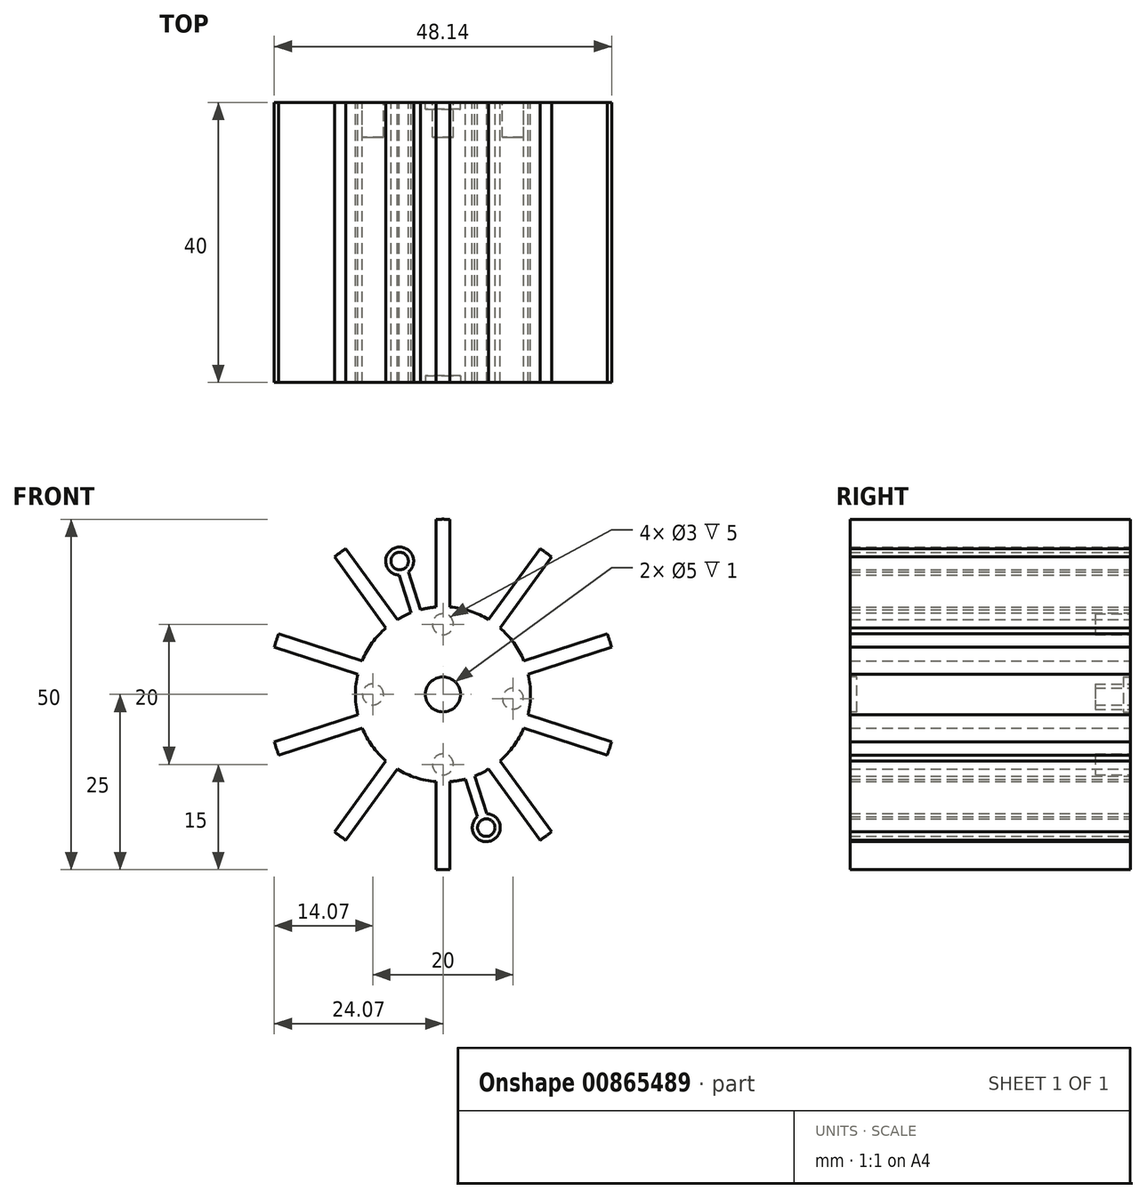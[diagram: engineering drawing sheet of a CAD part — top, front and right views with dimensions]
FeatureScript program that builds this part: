
annotation { "Feature Type Name" : "Feature", "Feature Type Description" : "" }
export const myFeature = defineFeature(function(context is Context, id is Id, definition is map)
    precondition{}
    {
        {
            var Q0;
            Q0=qCreatedBy(makeId("Front.planeOp"),FACE);
            var sketch = newSketch(context, id + "F0", { "sketchPlane" : qUnion([Q0])});
            skCircle(sketch, "E0", {"center": v(0, 0) * mm, "radius": 25 * mm});
            skSolve(sketch);
        }
        {
            var Q0;
            Q0 = qSketchRegion(id + "F0", true);
            extrude(context, id + "F1", {"entities" : qUnion([Q0]), "depth" : 40 * mm, "offsetDistance" : 25 * mm});
        }
        {
            var Q0;
            Q0=makeQuery(id+"F1.opExtrude","CAP_FACE",FACE,{"disambiguationData":[OSD([sQuery(id+"F0.wireOp",EDGE,"E0")])],"isStart":true});
            var sketch = newSketch(context, id + "F2", { "sketchPlane" : qUnion([Q0])});
            skCircle(sketch, "E1", {"center": v(0, 0) * mm, "radius": 2.5 * mm});
            skSolve(sketch);
        }
        {
            var Q0;
            Q0 = qSketchRegion(id + "F2", true);
            extrude(context, id + "F3", {"entities" : qUnion([Q0]), "operationType" : NewBodyOperationType.REMOVE, "oppositeDirection" : true, "depth" : 1 * mm, "offsetDistance" : 25 * mm});
        }
        {
            var Q0;
            Q0=makeQuery(id+"F1.opExtrude","CAP_FACE",FACE,{"disambiguationData":[OSD([sQuery(id+"F0.wireOp",EDGE,"E0")])],"isStart":true});
            var sketch = newSketch(context, id + "F4", { "sketchPlane" : qUnion([Q0])});
            skCircle(sketch, "E2", {"center": v(0, 0) * mm, "radius": 12.5 * mm});
            skLineSegment(sketch, "E3", {"start": v(1, 12.46) * mm, "end": v(1, 24.98) * mm});
            skLineSegment(sketch, "E4", {"start": v(-1, 12.46) * mm, "end": v(-1, 24.98) * mm});
            skLineSegment(sketch, "E5.1.0", {"start": v(-6.51, 10.67) * mm, "end": v(-13.87, 20.8) * mm});
            skLineSegment(sketch, "E5.1.1", {"start": v(-8.13, 9.5) * mm, "end": v(-15.5, 19.62) * mm});
            skLineSegment(sketch, "E5.2.0", {"start": v(-11.54, 4.8) * mm, "end": v(-23.45, 8.67) * mm});
            skLineSegment(sketch, "E5.2.1", {"start": v(-12.16, 2.9) * mm, "end": v(-24.07, 6.77) * mm});
            skLineSegment(sketch, "E5.3.0", {"start": v(-12.16, -2.9) * mm, "end": v(-24.07, -6.77) * mm});
            skLineSegment(sketch, "E5.3.1", {"start": v(-11.54, -4.8) * mm, "end": v(-23.45, -8.67) * mm});
            skLineSegment(sketch, "E5.4.0", {"start": v(-8.13, -9.5) * mm, "end": v(-15.5, -19.62) * mm});
            skLineSegment(sketch, "E5.4.1", {"start": v(-6.51, -10.67) * mm, "end": v(-13.87, -20.8) * mm});
            skLineSegment(sketch, "E5.5.0", {"start": v(-1, -12.46) * mm, "end": v(-1, -24.98) * mm});
            skLineSegment(sketch, "E5.5.1", {"start": v(1, -12.46) * mm, "end": v(1, -24.98) * mm});
            skLineSegment(sketch, "E5.6.0", {"start": v(6.51, -10.67) * mm, "end": v(13.87, -20.8) * mm});
            skLineSegment(sketch, "E5.6.1", {"start": v(8.13, -9.5) * mm, "end": v(15.5, -19.62) * mm});
            skLineSegment(sketch, "E5.7.0", {"start": v(11.54, -4.8) * mm, "end": v(23.45, -8.67) * mm});
            skLineSegment(sketch, "E5.7.1", {"start": v(12.16, -2.9) * mm, "end": v(24.07, -6.77) * mm});
            skLineSegment(sketch, "E5.8.0", {"start": v(12.16, 2.9) * mm, "end": v(24.07, 6.77) * mm});
            skLineSegment(sketch, "E5.8.1", {"start": v(11.54, 4.8) * mm, "end": v(23.45, 8.67) * mm});
            skLineSegment(sketch, "E5.9.0", {"start": v(8.13, 9.5) * mm, "end": v(15.5, 19.62) * mm});
            skLineSegment(sketch, "E5.9.1", {"start": v(6.51, 10.67) * mm, "end": v(13.87, 20.8) * mm});
            skCircle(sketch, "E6", {"center": v(0, 0) * mm, "radius": 25 * mm});
            skSolve(sketch);
        }
        {
            var Q0;
            {var subQ0=sQuery(id+"F4.wireOp",EDGE,"E5.8.1");Q0=makeQuery(id+"F4.imprint","IMPRINT",FACE,{"disambiguationData":[TD([[makeQuery(id+"F4.imprint","IMPRINT",EDGE,{"derivedFrom":subQ0}),1.0]])]});}
            var Q1;
            {var subQ0=sQuery(id+"F4.wireOp",EDGE,"E3");Q1=makeQuery(id+"F4.imprint","IMPRINT",FACE,{"disambiguationData":[TD([[makeQuery(id+"F4.imprint","IMPRINT",EDGE,{"derivedFrom":subQ0}),-1.0]])]});}
            var Q2;
            {var subQ0=sQuery(id+"F4.wireOp",EDGE,"E4");Q2=makeQuery(id+"F4.imprint","IMPRINT",FACE,{"disambiguationData":[TD([[makeQuery(id+"F4.imprint","IMPRINT",EDGE,{"derivedFrom":subQ0}),1.0]])]});}
            var Q3;
            {var subQ0=sQuery(id+"F4.wireOp",EDGE,"E5.1.1");Q3=makeQuery(id+"F4.imprint","IMPRINT",FACE,{"disambiguationData":[TD([[makeQuery(id+"F4.imprint","IMPRINT",EDGE,{"derivedFrom":subQ0}),1.0]])]});}
            var Q4;
            {var subQ0=sQuery(id+"F4.wireOp",EDGE,"E5.2.1");Q4=makeQuery(id+"F4.imprint","IMPRINT",FACE,{"disambiguationData":[TD([[makeQuery(id+"F4.imprint","IMPRINT",EDGE,{"derivedFrom":subQ0}),1.0]])]});}
            var Q5;
            {var subQ0=sQuery(id+"F4.wireOp",EDGE,"E5.3.1");Q5=makeQuery(id+"F4.imprint","IMPRINT",FACE,{"disambiguationData":[TD([[makeQuery(id+"F4.imprint","IMPRINT",EDGE,{"derivedFrom":subQ0}),1.0]])]});}
            var Q6;
            {var subQ0=sQuery(id+"F4.wireOp",EDGE,"E5.4.1");Q6=makeQuery(id+"F4.imprint","IMPRINT",FACE,{"disambiguationData":[TD([[makeQuery(id+"F4.imprint","IMPRINT",EDGE,{"derivedFrom":subQ0}),1.0]])]});}
            var Q7;
            {var subQ0=sQuery(id+"F4.wireOp",EDGE,"E5.5.1");Q7=makeQuery(id+"F4.imprint","IMPRINT",FACE,{"disambiguationData":[TD([[makeQuery(id+"F4.imprint","IMPRINT",EDGE,{"derivedFrom":subQ0}),1.0]])]});}
            var Q8;
            {var subQ0=sQuery(id+"F4.wireOp",EDGE,"E5.6.1");Q8=makeQuery(id+"F4.imprint","IMPRINT",FACE,{"disambiguationData":[TD([[makeQuery(id+"F4.imprint","IMPRINT",EDGE,{"derivedFrom":subQ0}),1.0]])]});}
            var Q9;
            {var subQ0=sQuery(id+"F4.wireOp",EDGE,"E5.7.1");Q9=makeQuery(id+"F4.imprint","IMPRINT",FACE,{"disambiguationData":[TD([[makeQuery(id+"F4.imprint","IMPRINT",EDGE,{"derivedFrom":subQ0}),1.0]])]});}
            extrude(context, id + "F5", {"entities" : qUnion([Q0, Q1, Q2, Q3, Q4, Q5, Q6, Q7, Q8, Q9]), "operationType" : NewBodyOperationType.REMOVE, "endBound" : BoundingType.THROUGH_ALL, "oppositeDirection" : true, "depth" : 25 * mm, "offsetDistance" : 25 * mm});
        }
        {
            var Q0;
            Q0=makeQuery(id+"F1.opExtrude","CAP_FACE",FACE,{"disambiguationData":[OSD([sQuery(id+"F0.wireOp",EDGE,"E0")])],"isStart":true});
            var sketch = newSketch(context, id + "F6", { "sketchPlane" : qUnion([Q0])});
            skLineSegment(sketch, "E7", {"start": v(0, 0) * mm, "end": v(7.78, 23.93) * mm});
            skLineSegment(sketch, "E8", {"start": v(3.2, 12.09) * mm, "end": v(5.51, 19.24) * mm});
            skLineSegment(sketch, "E9", {"start": v(5.51, 19.24) * mm, "end": v(6.85, 18.8) * mm});
            skLineSegment(sketch, "E10", {"start": v(6.85, 18.8) * mm, "end": v(4.52, 11.65) * mm});
            skCircle(sketch, "E11", {"center": v(6.18, 19.02) * mm, "radius": 2 * mm});
            skCircle(sketch, "E12", {"center": v(6.18, 19.02) * mm, "radius": 1.25 * mm});
            skLineSegment(sketch, "E13.1.0", {"start": v(-3.2, -12.09) * mm, "end": v(-5.51, -19.24) * mm});
            skLineSegment(sketch, "E13.1.1", {"start": v(-6.85, -18.8) * mm, "end": v(-4.52, -11.65) * mm});
            skCircle(sketch, "E13.1.2", {"center": v(-6.18, -19.02) * mm, "radius": 2 * mm});
            skCircle(sketch, "E13.1.3", {"center": v(-6.18, -19.02) * mm, "radius": 1.25 * mm});
            skPoint(sketch, "E13.center", {"position": v(0, 0) * mm});
            skCircle(sketch, "E14", {"center": v(0, 0) * mm, "radius": 12.5 * mm});
            skSolve(sketch);
        }
        {
            var Q0;
            Q0=makeQuery(id+"F6.imprint","IMPRINT",FACE,{"disambiguationData":[TD([[makeQuery(id+"F6.imprint","IMPRINT",EDGE,{"derivedFrom":makeQuery(id+"F3.boolean.opBoolean","COPY",EDGE,{"derivedFrom":makeQuery(id+"F3.opExtrude","CAP_EDGE",EDGE,{"disambiguationData":[OSD([sQuery(id+"F2.wireOp",EDGE,"E1")])],"isStart":true})})}),1.0]])]});
            var Q1;
            {var subQ0=sQuery(id+"F6.wireOp",EDGE,"E14");var subQ1=sQuery(id+"F6.wireOp",EDGE,"E13.1.0");var subQ2=makeQuery(id+"F6.imprint","INTERSECT",VERTEX,{"derivedFrom":[subQ1,subQ0]});Q1=makeQuery(id+"F6.imprint","IMPRINT",FACE,{"disambiguationData":[TD([[makeQuery(id+"F6.imprint","IMPRINT",EDGE,{"disambiguationData":[TD([[subQ2,-1.0]])],"derivedFrom":subQ1}),-1.0]])]});}
            var Q2;
            {var subQ0=sQuery(id+"F6.wireOp",EDGE,"E13.1.2");var subQ1=sQuery(id+"F6.wireOp",EDGE,"E13.1.0");var subQ2=makeQuery(id+"F6.imprint","INTERSECT",VERTEX,{"derivedFrom":[subQ1,subQ0]});Q2=makeQuery(id+"F6.imprint","IMPRINT",FACE,{"disambiguationData":[TD([[makeQuery(id+"F6.imprint","IMPRINT",EDGE,{"disambiguationData":[TD([[subQ2,-1.0]])],"derivedFrom":subQ1}),1.0]])]});}
            var Q3;
            {var subQ0=sQuery(id+"F6.wireOp",EDGE,"E14");var subQ1=sQuery(id+"F6.wireOp",EDGE,"E7");var subQ2=makeQuery(id+"F6.imprint","INTERSECT",VERTEX,{"derivedFrom":[subQ1,subQ0]});Q3=makeQuery(id+"F6.imprint","IMPRINT",FACE,{"disambiguationData":[TD([[makeQuery(id+"F6.imprint","IMPRINT",EDGE,{"disambiguationData":[TD([[subQ2,-1.0]])],"derivedFrom":subQ1}),1.0]])]});}
            var Q4;
            {var subQ0=sQuery(id+"F6.wireOp",EDGE,"E14");var subQ1=sQuery(id+"F6.wireOp",EDGE,"E7");var subQ2=makeQuery(id+"F6.imprint","INTERSECT",VERTEX,{"derivedFrom":[subQ1,subQ0]});Q4=makeQuery(id+"F6.imprint","IMPRINT",FACE,{"disambiguationData":[TD([[makeQuery(id+"F6.imprint","IMPRINT",EDGE,{"disambiguationData":[TD([[subQ2,-1.0]])],"derivedFrom":subQ1}),-1.0]])]});}
            var Q5;
            {var subQ0=sQuery(id+"F6.wireOp",EDGE,"E11");var subQ1=sQuery(id+"F6.wireOp",EDGE,"E7");var subQ2=makeQuery(id+"F6.imprint","INTERSECT",VERTEX,{"disambiguationData":[OD(0.0)],"derivedFrom":[subQ1,subQ0]});Q5=makeQuery(id+"F6.imprint","IMPRINT",FACE,{"disambiguationData":[TD([[makeQuery(id+"F6.imprint","IMPRINT",EDGE,{"disambiguationData":[TD([[subQ2,1.0]])],"derivedFrom":subQ1}),1.0]])]});}
            var Q6;
            {var subQ0=sQuery(id+"F6.wireOp",EDGE,"E11");var subQ1=sQuery(id+"F6.wireOp",EDGE,"E7");var subQ2=makeQuery(id+"F6.imprint","INTERSECT",VERTEX,{"disambiguationData":[OD(0.0)],"derivedFrom":[subQ1,subQ0]});Q6=makeQuery(id+"F6.imprint","IMPRINT",FACE,{"disambiguationData":[TD([[makeQuery(id+"F6.imprint","IMPRINT",EDGE,{"disambiguationData":[TD([[subQ2,1.0]])],"derivedFrom":subQ1}),-1.0]])]});}
            var Q7;
            {var subQ0=sQuery(id+"F6.wireOp",EDGE,"E13.1.2");var subQ1=sQuery(id+"F6.wireOp",EDGE,"E13.1.0");var subQ2=makeQuery(id+"F6.imprint","INTERSECT",VERTEX,{"derivedFrom":[subQ1,subQ0]});Q7=makeQuery(id+"F6.imprint","IMPRINT",FACE,{"disambiguationData":[TD([[makeQuery(id+"F6.imprint","IMPRINT",EDGE,{"disambiguationData":[TD([[subQ2,-1.0]])],"derivedFrom":subQ1}),-1.0]])]});}
            var Q8;
            {var subQ0=sQuery(id+"F6.wireOp",EDGE,"E11");var subQ1=sQuery(id+"F6.wireOp",EDGE,"E7");var subQ2=makeQuery(id+"F6.imprint","INTERSECT",VERTEX,{"disambiguationData":[OD(1.0)],"derivedFrom":[subQ1,subQ0]});Q8=makeQuery(id+"F6.imprint","IMPRINT",FACE,{"disambiguationData":[TD([[makeQuery(id+"F6.imprint","IMPRINT",EDGE,{"disambiguationData":[TD([[subQ2,-1.0]])],"derivedFrom":subQ1}),1.0]])]});}
            var Q9;
            {var subQ0=sQuery(id+"F6.wireOp",EDGE,"E11");var subQ1=sQuery(id+"F6.wireOp",EDGE,"E7");var subQ2=makeQuery(id+"F6.imprint","INTERSECT",VERTEX,{"disambiguationData":[OD(1.0)],"derivedFrom":[subQ1,subQ0]});Q9=makeQuery(id+"F6.imprint","IMPRINT",FACE,{"disambiguationData":[TD([[makeQuery(id+"F6.imprint","IMPRINT",EDGE,{"disambiguationData":[TD([[subQ2,-1.0]])],"derivedFrom":subQ1}),-1.0]])]});}
            extrude(context, id + "F7", {"entities" : qUnion([Q0, Q1, Q2, Q3, Q4, Q5, Q6, Q7, Q8, Q9]), "operationType" : NewBodyOperationType.ADD, "oppositeDirection" : true, "depth" : 40 * mm, "offsetDistance" : 25 * mm});
        }
        {
            var Q0;
            {var subQ0=sQuery(id+"F6.wireOp",EDGE,"E14");Q0=makeQuery(id+"F7.boolean.opBoolean","MERGE",FACE,{"derivedFrom":[makeQuery(id+"F1.opExtrude","CAP_FACE",FACE,{"disambiguationData":[OSD([sQuery(id+"F0.wireOp",EDGE,"E0")])],"isStart":false}),makeQuery(id+"F7.opExtrude","CAP_FACE",FACE,{"disambiguationData":[OSD([sQuery(id+"F6.wireOp",EDGE,"E8"),sQuery(id+"F6.wireOp",EDGE,"E10"),sQuery(id+"F6.wireOp",EDGE,"E11"),sQuery(id+"F6.wireOp",EDGE,"E12"),subQ0])],"isStart":false}),makeQuery(id+"F7.opExtrude","CAP_FACE",FACE,{"disambiguationData":[OSD([sQuery(id+"F6.wireOp",EDGE,"E13.1.0"),sQuery(id+"F6.wireOp",EDGE,"E13.1.1"),sQuery(id+"F6.wireOp",EDGE,"E13.1.2"),sQuery(id+"F6.wireOp",EDGE,"E13.1.3"),subQ0])],"isStart":false})]});}
            var sketch = newSketch(context, id + "F8", { "sketchPlane" : qUnion([Q0])});
            skCircle(sketch, "E15", {"center": v(0, 0) * mm, "radius": 2.5 * mm});
            skSolve(sketch);
        }
        {
            var Q0;
            Q0 = qSketchRegion(id + "F8", true);
            extrude(context, id + "F9", {"entities" : qUnion([Q0]), "operationType" : NewBodyOperationType.REMOVE, "oppositeDirection" : true, "depth" : 1 * mm, "offsetDistance" : 25 * mm});
        }
        {
            var Q0;
            {var subQ0=sQuery(id+"F6.wireOp",EDGE,"E14");Q0=makeQuery(id+"F7.boolean.opBoolean","MERGE",FACE,{"derivedFrom":[makeQuery(id+"F1.opExtrude","CAP_FACE",FACE,{"disambiguationData":[OSD([sQuery(id+"F0.wireOp",EDGE,"E0")])],"isStart":true}),makeQuery(id+"F7.opExtrude","CAP_FACE",FACE,{"disambiguationData":[OSD([sQuery(id+"F6.wireOp",EDGE,"E8"),sQuery(id+"F6.wireOp",EDGE,"E10"),sQuery(id+"F6.wireOp",EDGE,"E11"),sQuery(id+"F6.wireOp",EDGE,"E12"),subQ0])],"isStart":true}),makeQuery(id+"F7.opExtrude","CAP_FACE",FACE,{"disambiguationData":[OSD([sQuery(id+"F6.wireOp",EDGE,"E13.1.0"),sQuery(id+"F6.wireOp",EDGE,"E13.1.1"),sQuery(id+"F6.wireOp",EDGE,"E13.1.2"),sQuery(id+"F6.wireOp",EDGE,"E13.1.3"),subQ0])],"isStart":true}),makeQuery(id+"F7.opExtrude","CAP_FACE",FACE,{"disambiguationData":[OSD([sQuery(id+"F2.wireOp",EDGE,"E1")])],"isStart":true})]});}
            var sketch = newSketch(context, id + "F10", { "sketchPlane" : qUnion([Q0])});
            skCircle(sketch, "E16", {"center": v(10, 0) * mm, "radius": 1.5 * mm});
            skCircle(sketch, "E17", {"center": v(-10, -0.62) * mm, "radius": 1.5 * mm});
            skCircle(sketch, "E18", {"center": v(0, -10) * mm, "radius": 1.5 * mm});
            skCircle(sketch, "E19", {"center": v(0, 10) * mm, "radius": 1.5 * mm});
            skSolve(sketch);
        }
        {
            var Q0;
            Q0 = qSketchRegion(id + "F10", true);
            extrude(context, id + "F11", {"entities" : qUnion([Q0]), "operationType" : NewBodyOperationType.REMOVE, "oppositeDirection" : true, "depth" : 5 * mm, "offsetDistance" : 25 * mm});
        }
    });
